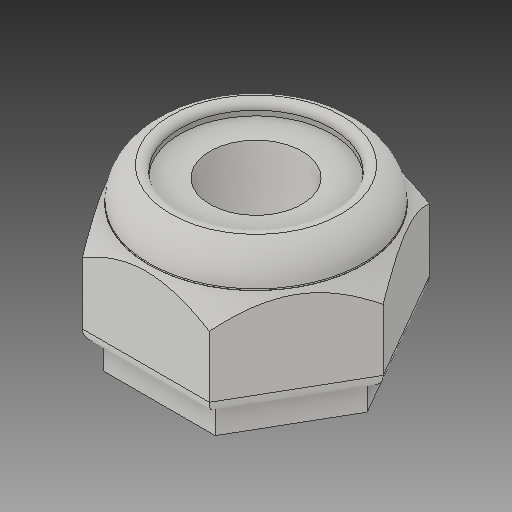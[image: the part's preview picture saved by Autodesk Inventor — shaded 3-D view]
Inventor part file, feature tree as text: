
AUTODESK INVENTOR PART (.ipt)
format: ipt  version: 2018 (Build 220112000, 112)  size: 167,424 bytes
history: native  units: in
note: dims shown in document units (in); Inventor stores cm internally (conversion verified against a paired STEP export)
features: extrude x1
ambient origin geometry x8: Origin, YZ Plane, XZ Plane, XY Plane, X Axis, Y Axis, Z Axis, Center Point
bodies: Solid1 (feature_tree)
feature tree (1):
  extrude  "Extrude1"  [1 undecoded]
note: 1 required parameter value undecoded (feature->parameter linkage not recoverable at this tier; creation-order binding heuristic only, values carry confidence <= 0.55)
